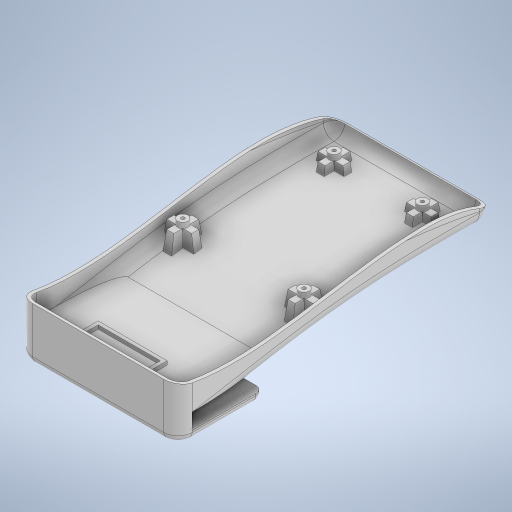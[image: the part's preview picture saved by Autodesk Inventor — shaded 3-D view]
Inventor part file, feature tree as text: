
AUTODESK INVENTOR PART (.ipt)
format: ipt  version: 2023 (Build 270158000, 158)  size: 1,330,176 bytes
history: native  units: mm
features: other x11, sketch x11, extrude x9, fillet x4, plane x2, split x2, shell x2
ambient origin geometry x8: Origin, YZ Plane, XZ Plane, XY Plane, X Axis, Y Axis, Z Axis, Center Point
bodies: Body1 (feature_tree), Body2 (feature_tree), Body3 (feature_tree), Body4 (feature_tree), Body5 (feature_tree)
feature tree (41):
  other  "Sólido1"
  extrude  "Extrusión1"  Depth=45.0mm
  sketch  "Boceto2"  dims[d5=45.0mm d12=4.0mm]
  sketch  "Boceto3"  dims[d13=27.0mm d14=4.0mm d15=4.5mm d16=25.5mm d17=4.5mm]
  fillet  "Empalme1"  Radius=24.0mm
  extrude  "Extrusión2"  Depth=4.0mm
  other  "Empalme de cara2"
  sketch  "Boceto6"  dims[d21=147.5mm d22=0.0mm d23=147.5mm d24=22.5mm d27=17.0mm]
  plane  "Plano de trabajo1"
  extrude  "Extrusión3"  Depth=4.0mm
  sketch  "Boceto8"  dims[d34=17.5mm d35=8.5mm]
  split  "Dividir3"
  fillet  "Empalme2"  Radius=4.5mm
  split  "Dividir4"
  shell  "Vaciado5"  Thickness=25.5mm
  shell  "Vaciado6"  Thickness=4.5mm
  extrude  "Extrusión4"  Depth=67.0mm
  extrude  "Extrusión5"  Depth=147.5mm
  fillet  "Empalme3"  Radius=22.5mm
  fillet  "Empalme4"  Radius=17.0mm
  plane  "Plano de trabajo2"
  other  "Soporte para fiador1"
  sketch  "Boceto14"  dims[d43=53.0mm d44=0.0mm d45=0.0mm d46=4.0mm d51=3.75mm d52=50.25mm d53=0.0mm d54=0.0mm d55=1.0mm d56=1.0mm d57=7.0mm d58=0.0mm d59=2.5mm d60=20.0mm d61=0.0mm d62=2.0mm d63=2.0mm d76=9.0mm d77=60.0mm d78=39.0mm d81=27.0mm d83=24.9mm d84=6.65mm d85=6.95mm d86=34.2mm d87=2.45mm d88=15.5mm d89=0.0mm d90=0.0mm d91=2.95mm d92=1.0mm d93=9.5mm d94=0.0mm d95=0.174533mm d96=40.0mm d98=2.0mm d99=1.5mm d100=3.5mm d101=0.0mm d102=1.745329mm d103=0.436332mm d104=0.0mm d105=0.0mm d106=0.0mm d107=360.0deg d108=0.0mm d109=0.0mm d110=3.5mm d111=1.0mm d112=9.5mm d113=0.349066mm d114=0.174533mm d115=20.0mm d117=2.0mm d118=2.0mm d119=10.0mm d120=0.0mm d121=1.745329mm d122=0.436332mm d123=0.0mm d124=0.0mm d125=0.0mm d126=360.0deg d127=10.0mm d128=0.0mm d129=5.5mm d130=7.0mm d135=6.5mm d136=6.5mm d137=10.0mm d138=0.0mm d139=4.0mm d142=1.0mm d143=0.5mm d144=1.0mm d145=0.5mm d146=1.0mm d147=0.5mm d148=1.0mm d149=0.5mm d150=0.0mm d151=0.0mm d153=8.4mm d154=13.6mm d167=7.0mm d168=0.0mm d169=0.0mm d170=84.5mm d171=1.0mm d131=0.5mm d132=0.872665mm]
  other  "Soporte para fiador2"
  extrude  "Extrusión8"  [1 undecoded]
  extrude  "Extrusión6"  Depth=8.5mm
  extrude  "Extrusión7"  Depth=32.5mm
  extrude  "Extrusión9"  Depth=42.5mm
  sketch  "Boceto1"  dims[d0=89.0mm d1=45.0mm d2=24.0mm d3=0.0mm]
  sketch  "Boceto4"  dims[d18=18.3mm d19=67.0mm]
  sketch  "Boceto7"  dims[d32=4.0mm d33=-1.0mm]
  other  "Sup3"
  sketch  "Boceto9"  dims[d36=1.5mm d37=32.5mm]
  other  "Sup4"
  sketch  "Boceto10"  dims[d38=0.0mm d39=0.0mm d40=42.5mm]
  sketch  "Boceto11"  dims[d41=28.333333mm]
  other  "Sólido4"
  other  "SuperficieBarrido3"
  other  "SuperficieExtrusión1"
  other  "Sólido2"
  other  "Sólido3"
note: 1 required parameter value undecoded (feature->parameter linkage not recoverable at this tier; creation-order binding heuristic only, values carry confidence <= 0.55)
